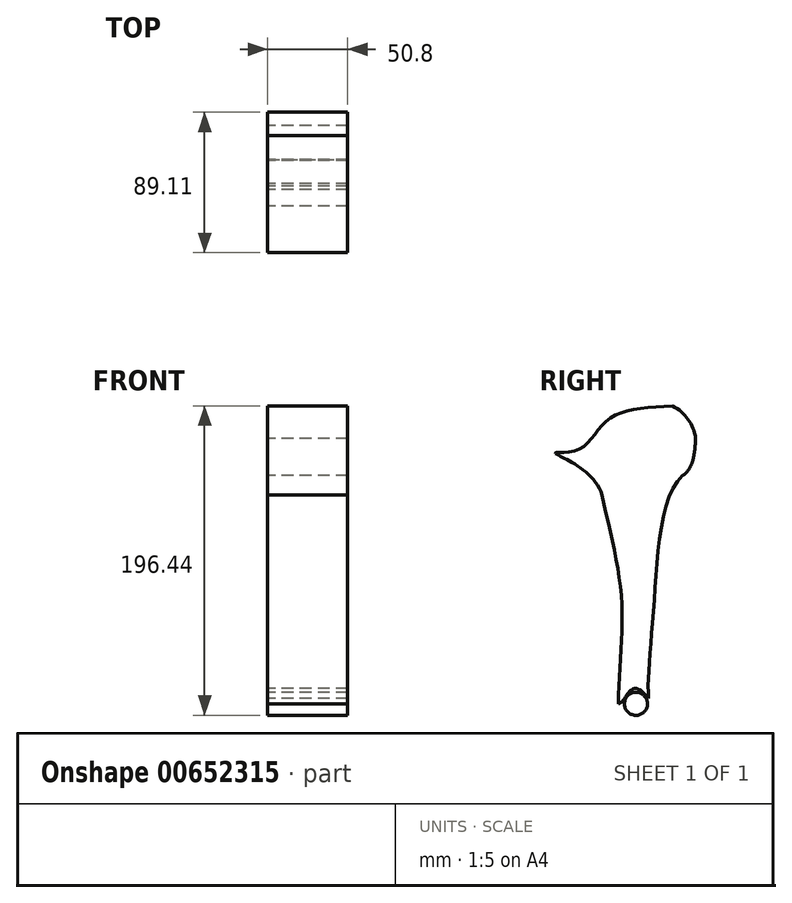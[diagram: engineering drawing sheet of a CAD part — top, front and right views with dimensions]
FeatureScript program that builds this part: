
annotation { "Feature Type Name" : "Feature", "Feature Type Description" : "" }
export const myFeature = defineFeature(function(context is Context, id is Id, definition is map)
    precondition{}
    {
        {
            var Q0;
            Q0=qCreatedBy(makeId("Right.planeOp"),FACE);
            var sketch = newSketch(context, id + "F0", { "sketchPlane" : qUnion([Q0])});
            skFitSpline(sketch, "E0", {"points": [v(50.95, 66.48) * mm, v(32.87, -16.8) * mm, v(29.57, -75.08) * mm], "startDerivative": vector(-79.87, -73.4) * mm, "endDerivative": vector(7.79, -83.06) * mm});
            skArc(sketch, "E1", {"start": v(50.95, 66.48) * mm, "mid": v(59.47, 90.21) * mm, "end": v(44.8, 110.72) * mm});
            skFitSpline(sketch, "E2", {"points": [v(44.8, 110.72) * mm, v(3.14, 101.56) * mm, v(-15.7, 82.8) * mm, v(-29.64, 80.79) * mm, v(-0.13, 54.3) * mm], "startDerivative": vector(-179.17, -6.41) * mm, "endDerivative": vector(48.82, -174.94) * mm});
            skFitSpline(sketch, "E3", {"points": [v(-0.13, 54.3) * mm, v(12.45, -13.27) * mm, v(10.38, -78.4) * mm], "startDerivative": vector(30.97, -137.23) * mm, "endDerivative": vector(-1.21, -131) * mm});
            skCircle(sketch, "E4", {"center": v(21.55, -78.4) * mm, "radius": 7.33 * mm});
            skFitSpline(sketch, "E5", {"points": [v(10.38, -78.4) * mm, v(29.57, -75.08) * mm], "startDerivative": vector(17.9, 4.91) * mm, "endDerivative": vector(35.13, -46.36) * mm});
            skLineSegment(sketch, "E6", {"start": v(10.38, -78.4) * mm, "end": v(29.57, -75.08) * mm});
            skLineSegment(sketch, "E7", {"start": v(28.68, -80.08) * mm, "end": v(25.58, -93.02) * mm});
            skLineSegment(sketch, "E8", {"start": v(25.58, -93.02) * mm, "end": v(20.75, -101.3) * mm});
            skLineSegment(sketch, "E9", {"start": v(14.98, -81.63) * mm, "end": v(16.92, -92.12) * mm});
            skFitSpline(sketch, "E10", {"points": [v(17.3, -94.14) * mm, v(3.15, -96.47) * mm, v(9.36, -104.58) * mm, v(20.75, -101.3) * mm], "startDerivative": vector(-54.94, 1.85) * mm, "endDerivative": vector(34.66, 21.16) * mm});
            skFitSpline(sketch, "E11", {"points": [v(-29.64, 80.79) * mm, v(50.95, 66.48) * mm, v(59.47, 90.21) * mm], "startDerivative": vector(157.92, -50.78) * mm, "endDerivative": vector(5.77, 82.32) * mm});
            skSolve(sketch);
        }
        {
            var Q0;
            {var subQ0=sQuery(id+"F0.wireOp",EDGE,"E11");var subQ1=sQuery(id+"F0.wireOp",EDGE,"E1");var subQ3=makeQuery(id+"F0.imprint","INTERSECT",VERTEX,{"disambiguationData":[OD(1.0)],"derivedFrom":[subQ1,subQ0]});Q0=makeQuery(id+"F0.imprint","IMPRINT",FACE,{"disambiguationData":[TD([[makeQuery(id+"F0.imprint","IMPRINT",EDGE,{"disambiguationData":[TD([[subQ3,1.0]])],"derivedFrom":subQ1}),-1.0]])]});}
            var Q1;
            {var subQ1=sQuery(id+"F0.wireOp",EDGE,"E1");var subQ3=sQuery(id+"F0.wireOp",EDGE,"E2");var subQ5=makeQuery(id+"F0.imprint","INTERSECT",VERTEX,{"derivedFrom":[subQ1,subQ3]});Q1=makeQuery(id+"F0.imprint","IMPRINT",FACE,{"disambiguationData":[TD([[makeQuery(id+"F0.imprint","IMPRINT",EDGE,{"disambiguationData":[TD([[subQ5,1.0]])],"derivedFrom":subQ1}),1.0]])]});}
            var Q2;
            {var subQ0=sQuery(id+"F0.wireOp",EDGE,"E0");Q2=makeQuery(id+"F0.imprint","IMPRINT",FACE,{"disambiguationData":[TD([[makeQuery(id+"F0.imprint","IMPRINT",EDGE,{"derivedFrom":subQ0}),-1.0]])]});}
            var Q3;
            {var subQ0=sQuery(id+"F0.wireOp",EDGE,"E4");var subQ5=makeQuery(id+"F0.imprint","IMPRINT",VERTEX,{"disambiguationData":[OD(0.0)],"derivedFrom":subQ0});Q3=makeQuery(id+"F0.imprint","IMPRINT",FACE,{"disambiguationData":[TD([[makeQuery(id+"F0.imprint","IMPRINT",EDGE,{"disambiguationData":[TD([[subQ5,1.0]])],"derivedFrom":subQ0}),1.0]])]});}
            var Q4;
            {var subQ0=sQuery(id+"F0.wireOp",EDGE,"E6");var subQ1=sQuery(id+"F0.wireOp",EDGE,"E4");var subQ2=makeQuery(id+"F0.imprint","INTERSECT",VERTEX,{"disambiguationData":[OD(0.0)],"derivedFrom":[subQ1,subQ0]});Q4=makeQuery(id+"F0.imprint","IMPRINT",FACE,{"disambiguationData":[TD([[makeQuery(id+"F0.imprint","IMPRINT",EDGE,{"disambiguationData":[TD([[subQ2,1.0]])],"derivedFrom":subQ1}),1.0]])]});}
            extrude(context, id + "F1", {"entities" : qUnion([Q0, Q1, Q2, Q3, Q4]), "depth" : 50.8 * mm, "offsetDistance" : 25.4 * mm});
        }
    });
